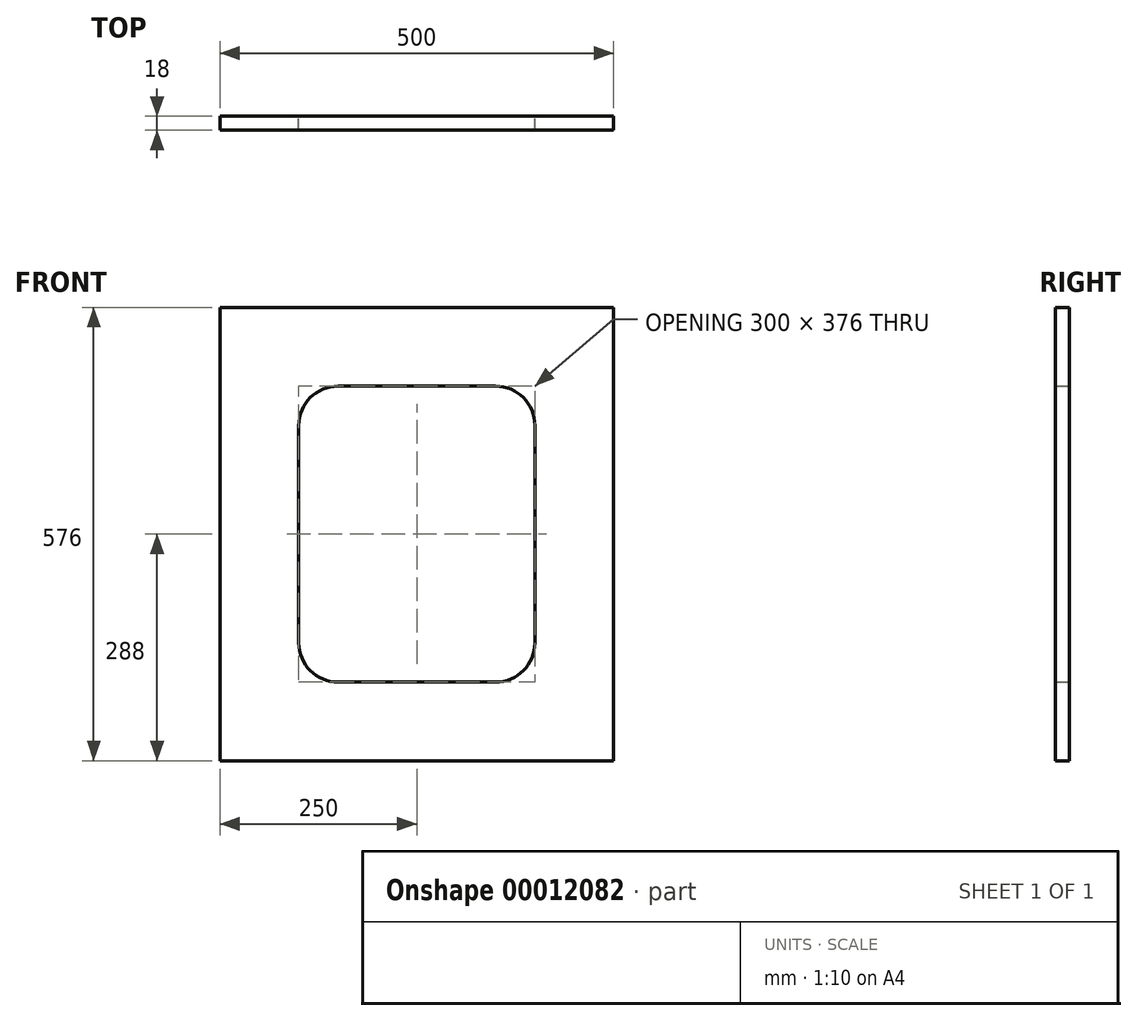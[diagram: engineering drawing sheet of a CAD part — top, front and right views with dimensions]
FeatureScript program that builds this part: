
annotation { "Feature Type Name" : "Feature", "Feature Type Description" : "" }
export const myFeature = defineFeature(function(context is Context, id is Id, definition is map)
    precondition{}
    {
        {
            var Q0;
            Q0=qCreatedBy(makeId("Front.planeOp"),FACE);
            var sketch = newSketch(context, id + "F0", { "sketchPlane" : qUnion([Q0])});
            skLineSegment(sketch, "E0.bottom", {"start": v(0, 0) * mm, "end": v(500, 0) * mm});
            skLineSegment(sketch, "E0.top", {"start": v(0, 576) * mm, "end": v(500, 576) * mm});
            skLineSegment(sketch, "E0.left", {"start": v(0, 0) * mm, "end": v(0, 576) * mm});
            skLineSegment(sketch, "E0.right", {"start": v(500, 0) * mm, "end": v(500, 576) * mm});
            skLineSegment(sketch, "E1.0", {"start": v(150, 476) * mm, "end": v(350, 476) * mm});
            skLineSegment(sketch, "E1.1", {"start": v(100, 150) * mm, "end": v(100, 426) * mm});
            skLineSegment(sketch, "E1.2", {"start": v(150, 100) * mm, "end": v(350, 100) * mm});
            skLineSegment(sketch, "E1.3", {"start": v(400, 150) * mm, "end": v(400, 426) * mm});
            skPoint(sketch, "E2.visualSharp", {"position": v(100, 476) * mm});
            skArc(sketch, "E2.filletArc", {"start": v(150, 476) * mm, "mid": v(114.64, 461.36) * mm, "end": v(100, 426) * mm});
            skPoint(sketch, "E3.visualSharp", {"position": v(400, 476) * mm});
            skArc(sketch, "E3.filletArc", {"start": v(400, 426) * mm, "mid": v(385.36, 461.36) * mm, "end": v(350, 476) * mm});
            skPoint(sketch, "E4.visualSharp", {"position": v(100, 100) * mm});
            skArc(sketch, "E4.filletArc", {"start": v(100, 150) * mm, "mid": v(114.64, 114.64) * mm, "end": v(150, 100) * mm});
            skPoint(sketch, "E5.visualSharp", {"position": v(400, 100) * mm});
            skArc(sketch, "E5.filletArc", {"start": v(350, 100) * mm, "mid": v(385.36, 114.64) * mm, "end": v(400, 150) * mm});
            skSolve(sketch);
        }
        {
            var Q0;
            Q0 = qSketchRegion(id + "F0", true);
            extrude(context, id + "F1", {"entities" : qUnion([Q0]), "depth" : 18 * mm});
        }
    });
